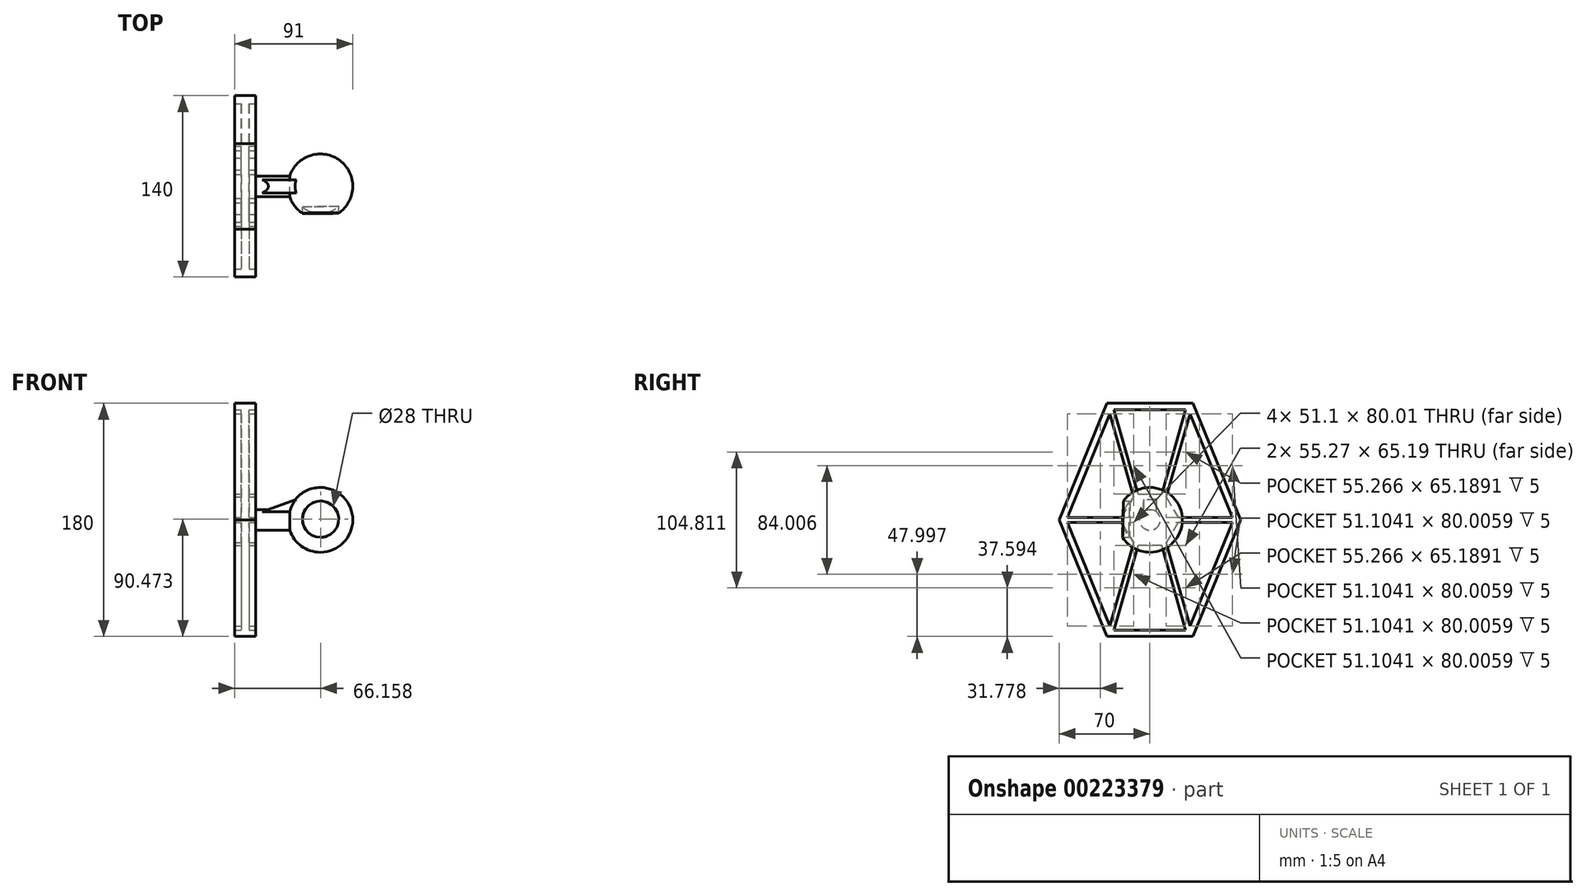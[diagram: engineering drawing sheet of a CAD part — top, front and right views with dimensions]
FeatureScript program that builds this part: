
annotation { "Feature Type Name" : "Feature", "Feature Type Description" : "" }
export const myFeature = defineFeature(function(context is Context, id is Id, definition is map)
    precondition{}
    {
        {
            var Q0;
            Q0=qCreatedBy(makeId("Front.planeOp"),FACE);
            var sketch = newSketch(context, id + "F0", { "sketchPlane" : qUnion([Q0])});
            skArc(sketch, "E0", {"start": v(0, -25) * mm, "mid": v(25, 0) * mm, "end": v(0, 25) * mm});
            skLineSegment(sketch, "E1", {"start": v(0, 25) * mm, "end": v(0, -25) * mm});
            skSolve(sketch);
        }
        {
            var Q0;
            Q0=qSketchRegion(id+"F0",true);
            var Q1;
            Q1=sQuery(id+"F0.wireOp",EDGE,"E1");
            revolve(context, id + "F1", {"entities" : qUnion([Q0]), "axis" : qUnion([Q1]), "revolveType" : RevolveType.FULL});
        }
        {
            var Q0;
            Q0=qCreatedBy(makeId("Front.planeOp"),FACE);
            var sketch = newSketch(context, id + "F2", { "sketchPlane" : qUnion([Q0])});
            skLineSegment(sketch, "E2.bottom", {"start": v(0, 0) * mm, "end": v(-55, 0) * mm});
            skLineSegment(sketch, "E2.top", {"start": v(0, 8) * mm, "end": v(-55, 8) * mm});
            skLineSegment(sketch, "E2.left", {"start": v(0, 0) * mm, "end": v(0, 8) * mm});
            skLineSegment(sketch, "E2.right", {"start": v(-55, 0) * mm, "end": v(-55, 8) * mm});
            skSolve(sketch);
        }
        {
            var Q0;
            Q0=qSketchRegion(id+"F2",true);
            var Q1;
            Q1=sQuery(id+"F2.wireOp",EDGE,"E2.bottom");
            revolve(context, id + "F3", {"operationType" : NewBodyOperationType.ADD, "entities" : qUnion([Q0]), "axis" : qUnion([Q1]), "revolveType" : RevolveType.FULL});
        }
        {
            var Q0;
            Q0=makeQuery(id+"F3.opRevolve","SWEPT_FACE",FACE,{"disambiguationData":[OSD([sQuery(id+"F2.wireOp",EDGE,"E2.right")])]});
            var sketch = newSketch(context, id + "F4", { "sketchPlane" : qUnion([Q0])});
            skLineSegment(sketch, "E3", {"start": v(0, 90) * mm, "end": v(-33.06, 90) * mm});
            skLineSegment(sketch, "E4", {"start": v(-33.06, 90) * mm, "end": v(-70, 0) * mm});
            skLineSegment(sketch, "E5", {"start": v(-70, 0) * mm, "end": v(0, 0) * mm, "construction": true});
            skLineSegment(sketch, "E6", {"start": v(0, 0) * mm, "end": v(0, 90) * mm, "construction": true});
            skLineSegment(sketch, "E7.MirrorCS", {"start": v(-33.06, -90) * mm, "end": v(-70, 0) * mm});
            skLineSegment(sketch, "E8.MirrorCS", {"start": v(0, -90) * mm, "end": v(-33.06, -90) * mm});
            skLineSegment(sketch, "E9.MirrorCS", {"start": v(0, 90) * mm, "end": v(33.06, 90) * mm});
            skLineSegment(sketch, "E10.MirrorCS", {"start": v(33.06, 90) * mm, "end": v(70, 0) * mm});
            skLineSegment(sketch, "E11.MirrorCS", {"start": v(33.06, -90) * mm, "end": v(70, 0) * mm});
            skLineSegment(sketch, "E12.MirrorCS", {"start": v(0, -90) * mm, "end": v(33.06, -90) * mm});
            skSolve(sketch);
        }
        {
            var Q0;
            Q0=qSketchRegion(id+"F4",true);
            extrude(context, id + "F5", {"entities" : qUnion([Q0]), "operationType" : NewBodyOperationType.ADD, "depth" : 6 * mm});
        }
        {
            var Q0;
            Q0=makeQuery(id+"F5.opExtrude","CAP_FACE",FACE,{"disambiguationData":[OSD([sQuery(id+"F4.wireOp",EDGE,"E3"),sQuery(id+"F4.wireOp",EDGE,"E4"),sQuery(id+"F4.wireOp",EDGE,"E7.MirrorCS"),sQuery(id+"F4.wireOp",EDGE,"E8.MirrorCS"),sQuery(id+"F4.wireOp",EDGE,"E9.MirrorCS"),sQuery(id+"F4.wireOp",EDGE,"E10.MirrorCS"),sQuery(id+"F4.wireOp",EDGE,"E11.MirrorCS"),sQuery(id+"F4.wireOp",EDGE,"E12.MirrorCS")])],"isStart":false});
            var sketch = newSketch(context, id + "F6", { "sketchPlane" : qUnion([Q0])});
            skLineSegment(sketch, "E13.0", {"start": v(-30.94, 82) * mm, "end": v(-12.67, 17.68) * mm});
            skLineSegment(sketch, "E14.0", {"start": v(-27.63, 85) * mm, "end": v(-9.12, 19.81) * mm});
            skLineSegment(sketch, "E15.0", {"start": v(-63.77, -2) * mm, "end": v(-21.72, -2) * mm});
            skLineSegment(sketch, "E16.0", {"start": v(-63.77, 2) * mm, "end": v(-21.72, 2) * mm});
            skLineSegment(sketch, "E17", {"start": v(0, 0) * mm, "end": v(0, -57.76) * mm, "construction": true});
            skLineSegment(sketch, "E18", {"start": v(0, 0) * mm, "end": v(92.77, 0) * mm, "construction": true});
            skLineSegment(sketch, "E19.MirrorCS", {"start": v(63.77, -2) * mm, "end": v(21.72, -2) * mm});
            skLineSegment(sketch, "E20.MirrorCS", {"start": v(63.77, 2) * mm, "end": v(21.72, 2) * mm});
            skLineSegment(sketch, "E21.MirrorCS", {"start": v(30.94, 82) * mm, "end": v(12.67, 17.68) * mm});
            skLineSegment(sketch, "E22.MirrorCS", {"start": v(27.63, 85) * mm, "end": v(9.12, 19.81) * mm});
            skLineSegment(sketch, "E23.MirrorCS", {"start": v(-30.94, -82) * mm, "end": v(-12.67, -17.68) * mm});
            skLineSegment(sketch, "E24.MirrorCS", {"start": v(-27.63, -85) * mm, "end": v(-9.12, -19.81) * mm});
            skLineSegment(sketch, "E25.MirrorCS", {"start": v(27.63, -85) * mm, "end": v(9.12, -19.81) * mm});
            skLineSegment(sketch, "E26.MirrorCS", {"start": v(30.94, -82) * mm, "end": v(12.67, -17.68) * mm});
            skLineSegment(sketch, "E27.0", {"start": v(-9.12, 19.81) * mm, "end": v(9.12, 19.81) * mm});
            skLineSegment(sketch, "E27.1", {"start": v(12.67, 17.68) * mm, "end": v(21.72, 2) * mm});
            skLineSegment(sketch, "E27.2", {"start": v(21.72, -2) * mm, "end": v(12.67, -17.68) * mm});
            skLineSegment(sketch, "E27.3", {"start": v(9.12, -19.81) * mm, "end": v(-9.12, -19.81) * mm});
            skLineSegment(sketch, "E27.4", {"start": v(-12.67, -17.68) * mm, "end": v(-21.72, -2) * mm});
            skLineSegment(sketch, "E27.5", {"start": v(-21.72, 2) * mm, "end": v(-12.67, 17.68) * mm});
            skPoint(sketch, "E27.0.midPoint", {"position": v(0, 19.81) * mm});
            skPoint(sketch, "E28.end.orphan", {"position": v(-10.36, 9.54) * mm});
            skPoint(sketch, "E28.start.orphan", {"position": v(-6.97, 12.24) * mm});
            skPoint(sketch, "E29.orphan", {"position": v(-11.44, 19.81) * mm});
            skPoint(sketch, "E30.end.orphan", {"position": v(6.97, 12.24) * mm});
            skPoint(sketch, "E30.start.orphan", {"position": v(10.36, 9.54) * mm});
            skPoint(sketch, "E31.orphan", {"position": v(11.44, 19.81) * mm});
            skPoint(sketch, "E32.orphan", {"position": v(14.09, 2) * mm});
            skPoint(sketch, "E33.MirrorCS.end.orphan", {"position": v(14.09, -2) * mm});
            skPoint(sketch, "E34.end.orphan", {"position": v(10.36, -9.54) * mm});
            skPoint(sketch, "E35.orphan", {"position": v(6.97, -12.24) * mm});
            skPoint(sketch, "E36.end.orphan", {"position": v(-6.97, -12.24) * mm});
            skPoint(sketch, "E36.start.orphan", {"position": v(-10.36, -9.54) * mm});
            skPoint(sketch, "E37.end.orphan", {"position": v(-14.09, -2) * mm});
            skPoint(sketch, "E37.start.orphan", {"position": v(-14.09, 2) * mm});
            skLineSegment(sketch, "E38.0", {"start": v(-33.06, 90) * mm, "end": v(-70, 0) * mm});
            skLineSegment(sketch, "E38.1", {"start": v(-33.06, -90) * mm, "end": v(33.06, -90) * mm});
            skLineSegment(sketch, "E38.2", {"start": v(33.06, -90) * mm, "end": v(70, 0) * mm});
            skLineSegment(sketch, "E38.3", {"start": v(-70, 0) * mm, "end": v(-33.06, -90) * mm});
            skLineSegment(sketch, "E38.4", {"start": v(70, 0) * mm, "end": v(33.06, 90) * mm});
            skLineSegment(sketch, "E38.5", {"start": v(33.06, 90) * mm, "end": v(-33.06, 90) * mm});
            skLineSegment(sketch, "E39.0", {"start": v(27.63, 85) * mm, "end": v(-27.63, 85) * mm});
            skLineSegment(sketch, "E39.1", {"start": v(-63.77, -2) * mm, "end": v(-30.94, -82) * mm});
            skLineSegment(sketch, "E39.2", {"start": v(-27.63, -85) * mm, "end": v(27.63, -85) * mm});
            skLineSegment(sketch, "E39.3", {"start": v(-30.94, 82) * mm, "end": v(-63.77, 2) * mm});
            skLineSegment(sketch, "E39.4", {"start": v(30.94, -82) * mm, "end": v(63.77, -2) * mm});
            skLineSegment(sketch, "E39.5", {"start": v(63.77, 2) * mm, "end": v(30.94, 82) * mm});
            skPoint(sketch, "E40.orphan", {"position": v(-31.64, 84.45) * mm});
            skPoint(sketch, "E41.orphan", {"position": v(-27.79, 85.55) * mm});
            skPoint(sketch, "E42.orphan", {"position": v(31.64, 84.45) * mm});
            skPoint(sketch, "E43.orphan", {"position": v(27.79, 85.55) * mm});
            skPoint(sketch, "E44.orphan", {"position": v(64.6, 2) * mm});
            skPoint(sketch, "E45.MirrorCS.end.orphan", {"position": v(64.6, -2) * mm});
            skPoint(sketch, "E46.orphan", {"position": v(31.64, -84.45) * mm});
            skPoint(sketch, "E47.orphan", {"position": v(27.79, -85.55) * mm});
            skPoint(sketch, "E48.orphan", {"position": v(-31.64, -84.45) * mm});
            skPoint(sketch, "E49.orphan", {"position": v(-27.79, -85.55) * mm});
            skPoint(sketch, "E50.orphan", {"position": v(-64.6, 2) * mm});
            skPoint(sketch, "E51.orphan", {"position": v(-64.6, -2) * mm});
            skSolve(sketch);
        }
        {
            var Q0;
            Q0 = qSketchRegion(id + "F6", true);
            extrude(context, id + "F7", {"entities" : qUnion([Q0]), "operationType" : NewBodyOperationType.ADD, "depth" : 5 * mm, "hasSecondDirection" : true, "secondDirectionOppositeDirection" : true, "secondDirectionDepth" : 11 * mm});
        }
        {
            var Q0;
            Q0=qCreatedBy(makeId("Front.planeOp"),FACE);
            var sketch = newSketch(context, id + "F8", { "sketchPlane" : qUnion([Q0])});
            skLineSegment(sketch, "E52", {"start": v(-44.96, 6.15) * mm, "end": v(-11.83, 18.46) * mm});
            skLineSegment(sketch, "E53", {"start": v(-11.83, 18.46) * mm, "end": v(-11.83, 5.2) * mm});
            skLineSegment(sketch, "E54", {"start": v(-11.83, 5.2) * mm, "end": v(-44.96, 6.15) * mm});
            skSolve(sketch);
        }
        {
            var Q0;
            Q0=makeQuery(id+"F8.imprint","IMPRINT",FACE,{"disambiguationData":[TD([[makeQuery(id+"F8.imprint","IMPRINT",EDGE,{"derivedFrom":sQuery(id+"F8.wireOp",EDGE,"E52")}),-1.0]])]});
            extrude(context, id + "F9", {"entities" : qUnion([Q0]), "operationType" : NewBodyOperationType.ADD, "depth" : 5 * mm, "hasSecondDirection" : true, "secondDirectionOppositeDirection" : true, "secondDirectionDepth" : 5 * mm});
        }
        {
            var Q0;
            Q0=qCreatedBy(makeId("Front.planeOp"),FACE);
            var sketch = newSketch(context, id + "F10", { "sketchPlane" : qUnion([Q0])});
            skCircle(sketch, "E55", {"center": v(0.16, 0.47) * mm, "radius": 14 * mm});
            skSolve(sketch);
        }
        {
            var Q0;
            Q0 = qSketchRegion(id + "F10", true);
            extrude(context, id + "F11", {"entities" : qUnion([Q0]), "operationType" : NewBodyOperationType.REMOVE, "depth" : 25 * mm});
        }
        {
            var Q0;
            Q0=qCreatedBy(makeId("Front.planeOp"),FACE);
            var sketch = newSketch(context, id + "F12", { "sketchPlane" : qUnion([Q0])});
            skArc(sketch, "E56", {"start": v(-0.15, -20.84) * mm, "mid": v(20.84, 0.16) * mm, "end": v(-0.15, 21.16) * mm});
            skLineSegment(sketch, "E57", {"start": v(-0.15, 21.16) * mm, "end": v(-0.15, -20.84) * mm});
            skSolve(sketch);
        }
        {
            var Q0;
            Q0 = qSketchRegion(id + "F12", true);
            var Q1;
            Q1=sQuery(id+"F12.wireOp",EDGE,"E57");
            revolve(context, id + "F13", {"operationType" : NewBodyOperationType.ADD, "entities" : qUnion([Q0]), "axis" : qUnion([Q1]), "revolveType" : RevolveType.FULL});
        }
    });
